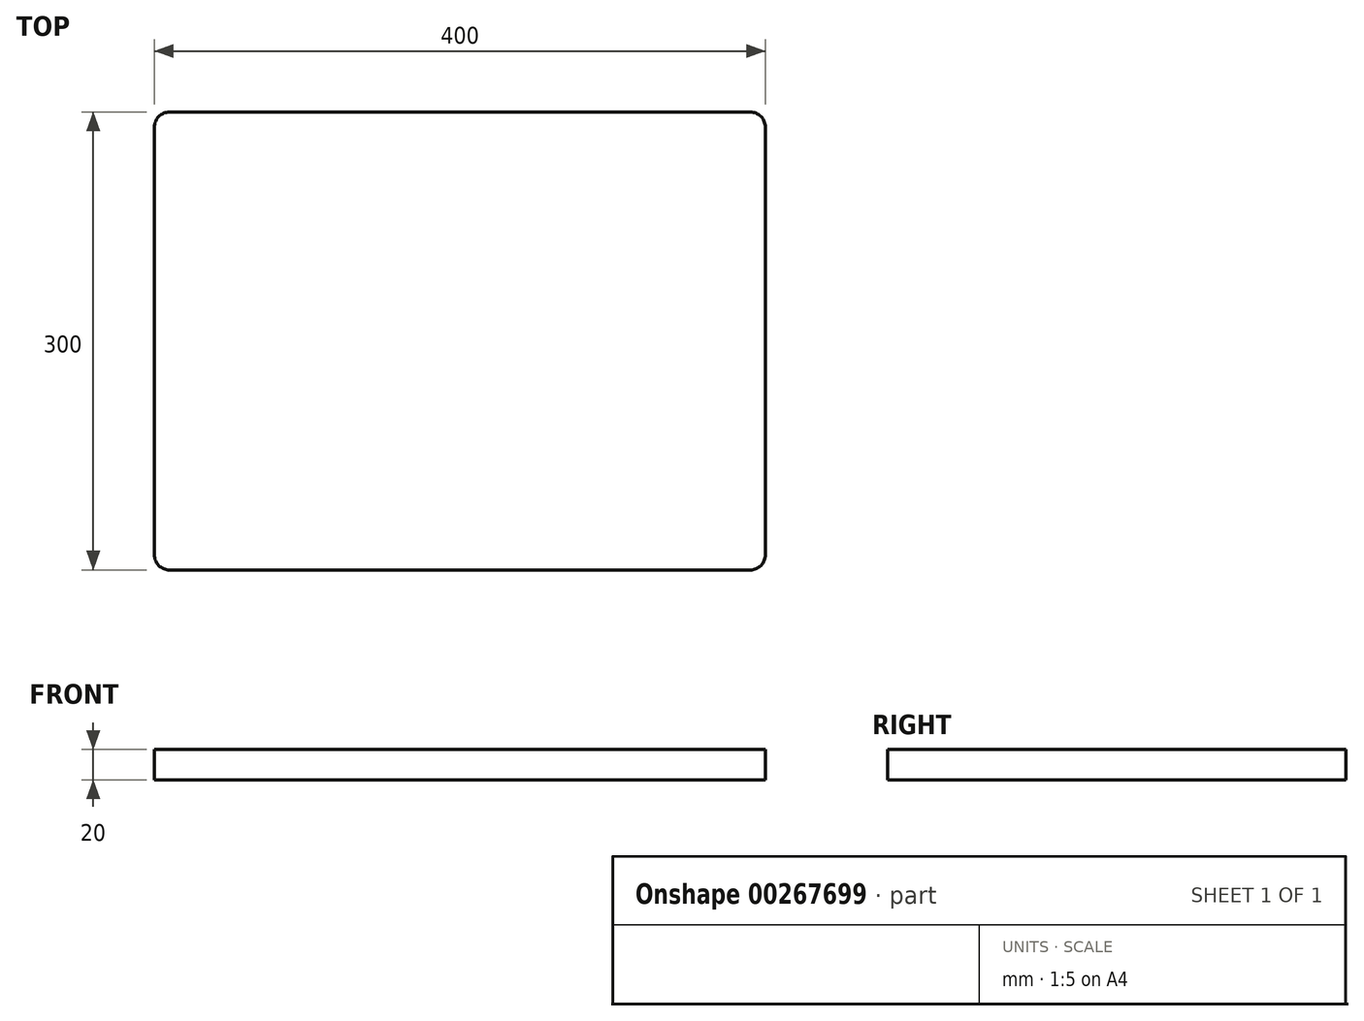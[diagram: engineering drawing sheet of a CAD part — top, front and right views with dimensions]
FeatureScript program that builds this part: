
annotation { "Feature Type Name" : "Feature", "Feature Type Description" : "" }
export const myFeature = defineFeature(function(context is Context, id is Id, definition is map)
    precondition{}
    {
        {
            var Q0;
            Q0=qCreatedBy(makeId("Top.planeOp"),FACE);
            var sketch = newSketch(context, id + "F0", { "sketchPlane" : qUnion([Q0])});
            skLineSegment(sketch, "E0.bottom", {"start": v(-190, 150) * mm, "end": v(190, 150) * mm});
            skLineSegment(sketch, "E0.top", {"start": v(-190, -150) * mm, "end": v(190, -150) * mm});
            skLineSegment(sketch, "E0.left", {"start": v(-200, 140) * mm, "end": v(-200, -140) * mm});
            skLineSegment(sketch, "E0.right", {"start": v(200, 140) * mm, "end": v(200, -140) * mm});
            skPoint(sketch, "E0.middle", {"position": v(0, 0) * mm});
            skPoint(sketch, "E1.visualSharp", {"position": v(-200, -150) * mm});
            skArc(sketch, "E1.filletArc", {"start": v(-200, -140) * mm, "mid": v(-197.07, -147.07) * mm, "end": v(-190, -150) * mm});
            skPoint(sketch, "E2.visualSharp", {"position": v(-200, 150) * mm});
            skArc(sketch, "E2.filletArc", {"start": v(-190, 150) * mm, "mid": v(-197.07, 147.07) * mm, "end": v(-200, 140) * mm});
            skPoint(sketch, "E3.visualSharp", {"position": v(200, 150) * mm});
            skArc(sketch, "E3.filletArc", {"start": v(200, 140) * mm, "mid": v(197.07, 147.07) * mm, "end": v(190, 150) * mm});
            skPoint(sketch, "E4.visualSharp", {"position": v(200, -150) * mm});
            skArc(sketch, "E4.filletArc", {"start": v(190, -150) * mm, "mid": v(197.07, -147.07) * mm, "end": v(200, -140) * mm});
            skSolve(sketch);
        }
        {
            var Q0;
            Q0=qSketchRegion(id+"F0",true);
            extrude(context, id + "F1", {"entities" : qUnion([Q0]), "oppositeDirection" : true, "depth" : 20 * mm});
        }
    });
